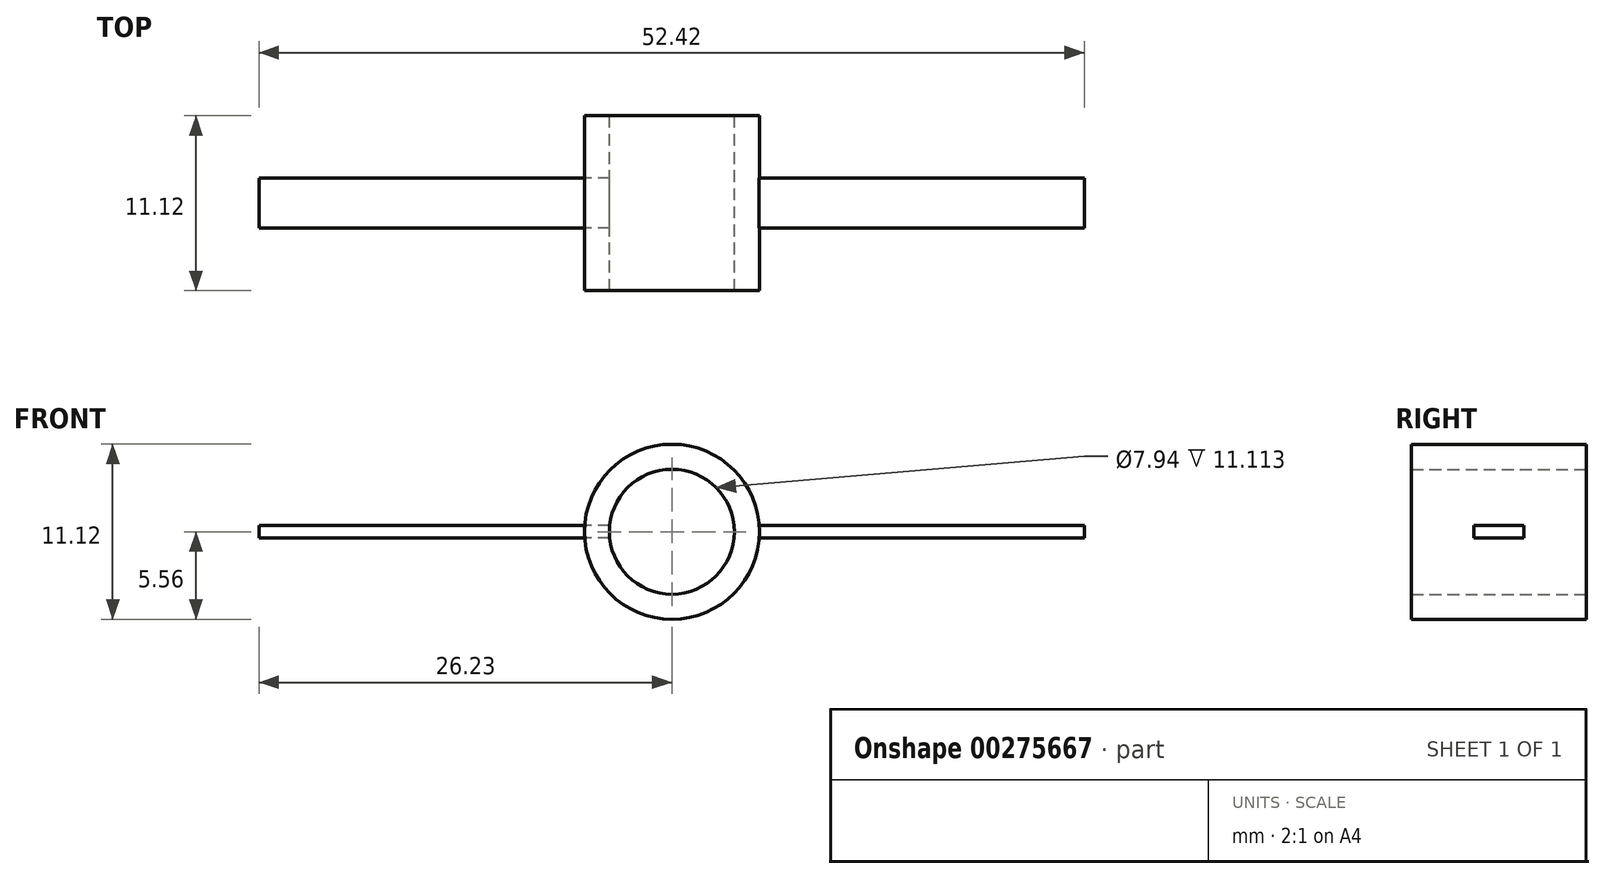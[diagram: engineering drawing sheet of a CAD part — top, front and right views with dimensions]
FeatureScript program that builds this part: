
annotation { "Feature Type Name" : "Feature", "Feature Type Description" : "" }
export const myFeature = defineFeature(function(context is Context, id is Id, definition is map)
    precondition{}
    {
        {
            var Q0;
            Q0=qCreatedBy(makeId("Front.planeOp"),FACE);
            var sketch = newSketch(context, id + "F0", { "sketchPlane" : qUnion([Q0])});
            skCircle(sketch, "E0", {"center": v(0, 0) * mm, "radius": 3.97 * mm});
            skCircle(sketch, "E1", {"center": v(0, 0) * mm, "radius": 5.56 * mm});
            skSolve(sketch);
        }
        {
            var Q0;
            Q0=makeQuery(id+"F0.imprint","IMPRINT",FACE,{"disambiguationData":[TD([[makeQuery(id+"F0.imprint","IMPRINT",EDGE,{"derivedFrom":sQuery(id+"F0.wireOp",EDGE,"E0")}),-1.0]])]});
            extrude(context, id + "F1", {"entities" : qUnion([Q0]), "depth" : 5.56 * mm});
        }
        {
            var Q0;
            Q0=qCreatedBy(makeId("Top.planeOp"),FACE);
            var sketch = newSketch(context, id + "F2", { "sketchPlane" : qUnion([Q0])});
            skLineSegment(sketch, "E2", {"start": v(0, 0) * mm, "end": v(17.66, 0) * mm, "construction": true});
            skLineSegment(sketch, "E3", {"start": v(5.56, 3.18) * mm, "end": v(5.56, 0) * mm, "construction": true});
            skLineSegment(sketch, "E4.top", {"start": v(5.56, -1.59) * mm, "end": v(26.2, -1.59) * mm});
            skLineSegment(sketch, "E5", {"start": v(5.56, -1.59) * mm, "end": v(5.56, 1.59) * mm});
            skPoint(sketch, "E5.endSnap0", {"position": v(5.56, 1.59) * mm});
            skLineSegment(sketch, "E6", {"start": v(5.56, 1.59) * mm, "end": v(26.2, 1.59) * mm});
            skLineSegment(sketch, "E7", {"start": v(26.2, 1.59) * mm, "end": v(26.2, -1.59) * mm});
            skLineSegment(sketch, "E8", {"start": v(-5.56, 3.8) * mm, "end": v(-5.56, 0) * mm, "construction": true});
            skLineSegment(sketch, "E9.top", {"start": v(-5.56, -1.59) * mm, "end": v(-26.23, -1.59) * mm});
            skLineSegment(sketch, "E10", {"start": v(-26.23, -1.59) * mm, "end": v(-26.23, 1.59) * mm});
            skLineSegment(sketch, "E11", {"start": v(-26.23, 1.59) * mm, "end": v(-5.56, 1.59) * mm});
            skPoint(sketch, "E11.endSnap0", {"position": v(-5.56, 1.9) * mm});
            skLineSegment(sketch, "E12", {"start": v(-5.56, 1.59) * mm, "end": v(-5.56, -1.59) * mm});
            skLineSegment(sketch, "E13", {"start": v(0, 0) * mm, "end": v(-15.62, 0) * mm, "construction": true});
            skSolve(sketch);
        }
        {
            var Q0;
            Q0=makeQuery(id+"F0.imprint","IMPRINT",FACE,{"disambiguationData":[TD([[makeQuery(id+"F0.imprint","IMPRINT",EDGE,{"derivedFrom":sQuery(id+"F0.wireOp",EDGE,"E0")}),-1.0]])]});
            extrude(context, id + "F3", {"entities" : qUnion([Q0]), "operationType" : NewBodyOperationType.ADD, "depth" : 5.56 * mm});
        }
        {
            var Q0;
            Q0=makeQuery(id+"F1.opExtrude","CAP_FACE",FACE,{"disambiguationData":[OSD([sQuery(id+"F0.wireOp",EDGE,"E0"),sQuery(id+"F0.wireOp",EDGE,"E1")])],"isStart":true});
            extrude(context, id + "F4", {"entities" : qUnion([Q0]), "operationType" : NewBodyOperationType.ADD, "depth" : 5.56 * mm});
        }
        {
            var Q0;
            Q0 = qSketchRegion(id + "F2", true);
            extrude(context, id + "F5", {"entities" : qUnion([Q0]), "depth" : 0.4 * mm});
        }
        {
            var Q0;
            Q0=makeQuery(id+"F5.opExtrude","CAP_FACE",FACE,{"disambiguationData":[OSD([sQuery(id+"F2.wireOp",EDGE,"E4.top"),sQuery(id+"F2.wireOp",EDGE,"E5"),sQuery(id+"F2.wireOp",EDGE,"E6"),sQuery(id+"F2.wireOp",EDGE,"E7")])],"isStart":true});
            extrude(context, id + "F6", {"entities" : qUnion([Q0]), "operationType" : NewBodyOperationType.ADD, "depth" : 0.4 * mm});
        }
        {
            var Q0;
            Q0=makeQuery(id+"F2.imprint","IMPRINT",FACE,{"disambiguationData":[TD([[makeQuery(id+"F2.imprint","IMPRINT",EDGE,{"derivedFrom":sQuery(id+"F2.wireOp",EDGE,"E9.top")}),-1.0]])]});
            extrude(context, id + "F7", {"entities" : qUnion([Q0]), "operationType" : NewBodyOperationType.ADD, "depth" : 0.4 * mm});
        }
        {
            var Q0;
            Q0=makeQuery(id+"F5.opExtrude","CAP_FACE",FACE,{"disambiguationData":[OSD([sQuery(id+"F2.wireOp",EDGE,"E9.top"),sQuery(id+"F2.wireOp",EDGE,"E10"),sQuery(id+"F2.wireOp",EDGE,"E11"),sQuery(id+"F2.wireOp",EDGE,"E12")])],"isStart":true});
            extrude(context, id + "F8", {"entities" : qUnion([Q0]), "operationType" : NewBodyOperationType.ADD, "depth" : 0.4 * mm});
        }
        {
            var Q0;
            {var subQ0=sQuery(id+"F2.wireOp",EDGE,"E5");Q0=makeQuery(id+"F6.boolean.opBoolean","MERGE",FACE,{"derivedFrom":[makeQuery(id+"F5.opExtrude","SWEPT_FACE",FACE,{"disambiguationData":[OSD([subQ0])]}),makeQuery(id+"F6.opExtrude","SWEPT_FACE",FACE,{"disambiguationData":[OSD([subQ0])]})]});}
            var Q1;
            Q1=makeQuery(id+"F1.opExtrude","SWEPT_BODY",BODY,{"disambiguationData":[OSD([sQuery(id+"F0.wireOp",EDGE,"E0"),sQuery(id+"F0.wireOp",EDGE,"E1")])]});
            extrude(context, id + "F9", {"entities" : qUnion([Q0]), "endBound" : BoundingType.UP_TO_NEXT, "endBoundEntityBody" : qUnion([Q1]), "depth" : 25.4 * mm});
        }
        {
            var Q0;
            {var subQ0=sQuery(id+"F2.wireOp",EDGE,"E12");Q0=makeQuery(id+"F8.boolean.opBoolean","MERGE",FACE,{"derivedFrom":[makeQuery(id+"F5.opExtrude","SWEPT_FACE",FACE,{"disambiguationData":[OSD([subQ0])]}),makeQuery(id+"F8.opExtrude","SWEPT_FACE",FACE,{"disambiguationData":[OSD([subQ0])]})]});}
            extrude(context, id + "F10", {"entities" : qUnion([Q0]), "endBound" : BoundingType.UP_TO_NEXT, "depth" : 25.4 * mm});
        }
        {
            var Q0;
            Q0=makeQuery(id+"F1.opExtrude","SWEPT_BODY",BODY,{"disambiguationData":[OSD([sQuery(id+"F0.wireOp",EDGE,"E0"),sQuery(id+"F0.wireOp",EDGE,"E1")])]});
            var Q1;
            Q1=makeQuery(id+"F5.opExtrude","SWEPT_BODY",BODY,{"disambiguationData":[OSD([sQuery(id+"F2.wireOp",EDGE,"E4.top"),sQuery(id+"F2.wireOp",EDGE,"E5"),sQuery(id+"F2.wireOp",EDGE,"E6"),sQuery(id+"F2.wireOp",EDGE,"E7")])]});
            var Q2;
            Q2=makeQuery(id+"F5.opExtrude","SWEPT_BODY",BODY,{"disambiguationData":[OSD([sQuery(id+"F2.wireOp",EDGE,"E9.top"),sQuery(id+"F2.wireOp",EDGE,"E10"),sQuery(id+"F2.wireOp",EDGE,"E11"),sQuery(id+"F2.wireOp",EDGE,"E12")])]});
            var Q3;
            Q3=makeQuery(id+"F9.opExtrude","SWEPT_BODY",BODY,{"disambiguationData":[OSD([sQuery(id+"F2.wireOp",EDGE,"E5")])]});
            booleanBodies(context, id + "F11", {"operationType" : BooleanOperationType.UNION, "tools" : qUnion([Q0, Q1, Q2, Q3])});
        }
    });
